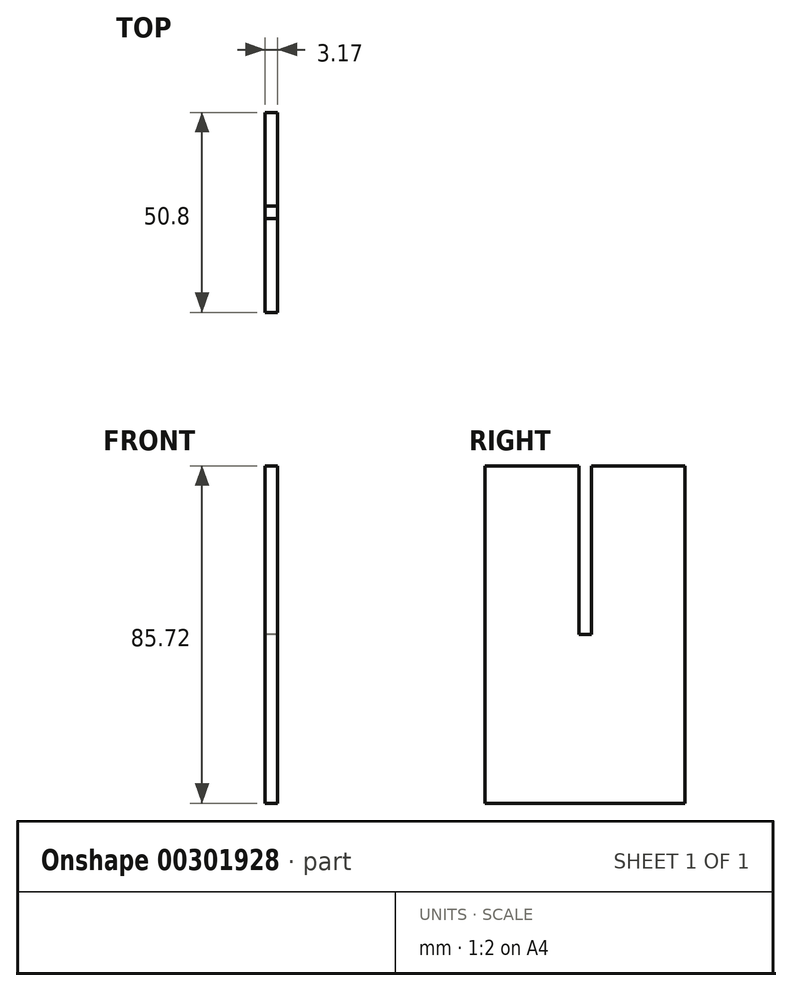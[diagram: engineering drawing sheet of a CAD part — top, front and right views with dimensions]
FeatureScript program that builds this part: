
annotation { "Feature Type Name" : "Feature", "Feature Type Description" : "" }
export const myFeature = defineFeature(function(context is Context, id is Id, definition is map)
    precondition{}
    {
        {
            var Q0;
            Q0=qCreatedBy(makeId("Right.planeOp"),FACE);
            var sketch = newSketch(context, id + "F0", { "sketchPlane" : qUnion([Q0])});
            skLineSegment(sketch, "E0.bottom", {"start": v(25.4, -42.86) * mm, "end": v(-25.4, -42.86) * mm});
            skLineSegment(sketch, "E0.top", {"start": v(25.4, 42.86) * mm, "end": v(-25.4, 42.86) * mm});
            skLineSegment(sketch, "E0.left", {"start": v(25.4, -42.86) * mm, "end": v(25.4, 42.86) * mm});
            skLineSegment(sketch, "E0.right", {"start": v(-25.4, -42.86) * mm, "end": v(-25.4, 42.86) * mm});
            skPoint(sketch, "E0.middle", {"position": v(0, 0) * mm});
            skLineSegment(sketch, "E1.bottom", {"start": v(-1.57, 42.86) * mm, "end": v(1.6, 42.86) * mm});
            skLineSegment(sketch, "E1.top", {"start": v(-1.57, 0.06) * mm, "end": v(1.6, 0.06) * mm});
            skLineSegment(sketch, "E1.left", {"start": v(-1.57, 42.86) * mm, "end": v(-1.57, 0.06) * mm});
            skLineSegment(sketch, "E1.right", {"start": v(1.6, 42.86) * mm, "end": v(1.6, 0.06) * mm});
            skSolve(sketch);
        }
        {
            var Q0;
            Q0=makeQuery(id+"F0.imprint","IMPRINT",FACE,{"disambiguationData":[TD([[makeQuery(id+"F0.imprint","IMPRINT",EDGE,{"derivedFrom":sQuery(id+"F0.wireOp",EDGE,"E0.bottom")}),-1.0]])]});
            extrude(context, id + "F1", {"entities" : qUnion([Q0]), "depth" : 3.17 * mm});
        }
    });
